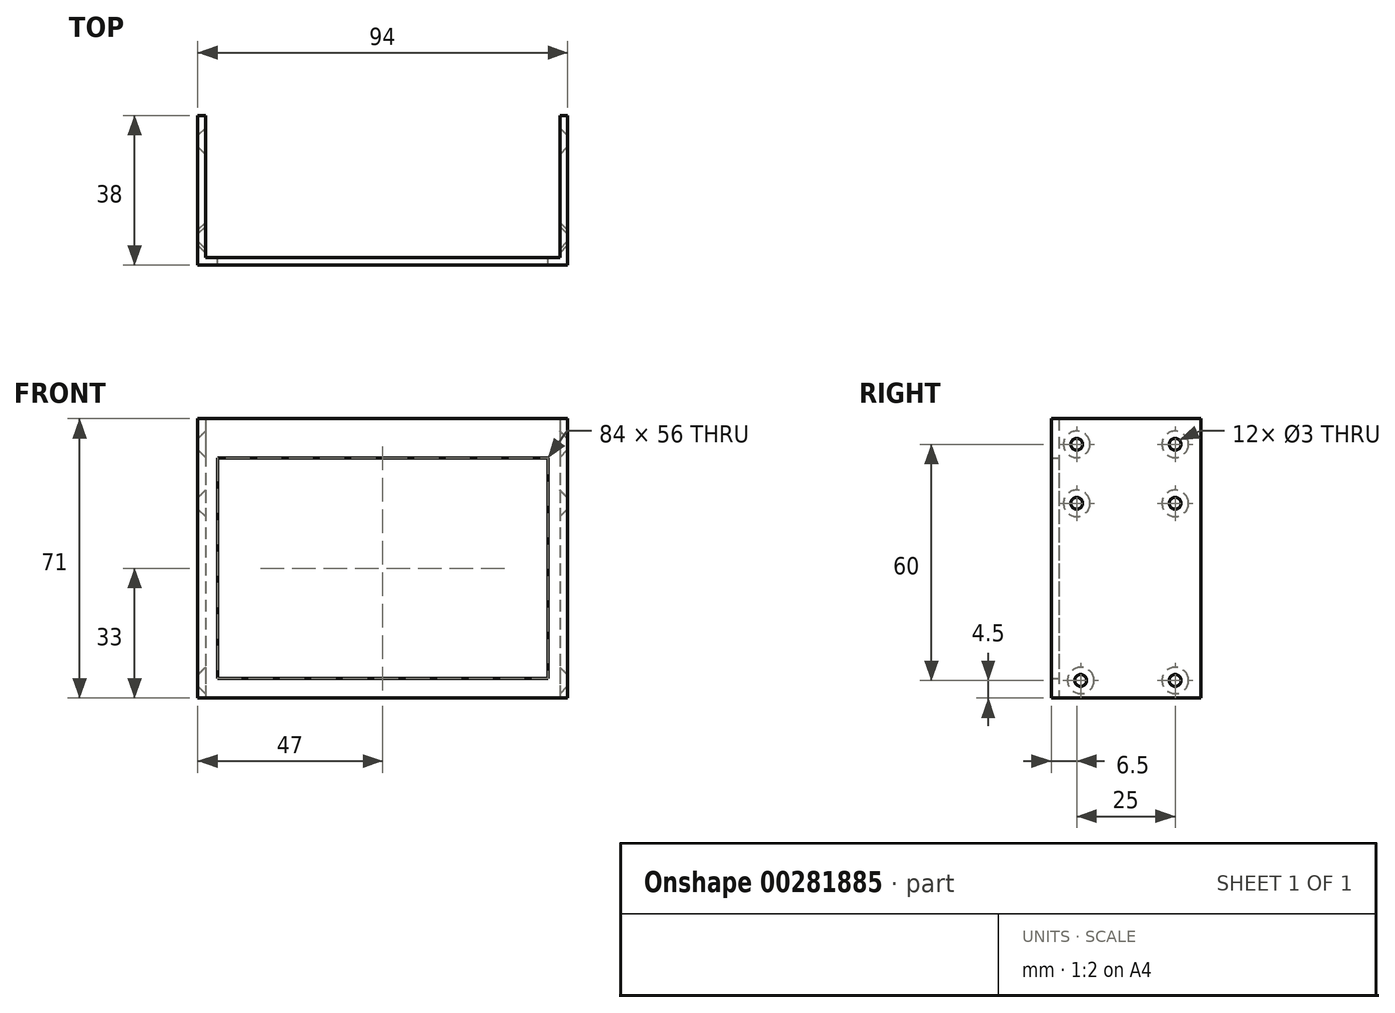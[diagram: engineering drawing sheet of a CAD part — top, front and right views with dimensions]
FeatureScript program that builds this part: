
annotation { "Feature Type Name" : "Feature", "Feature Type Description" : "" }
export const myFeature = defineFeature(function(context is Context, id is Id, definition is map)
    precondition{}
    {
        {
            var Q0;
            Q0=qCreatedBy(makeId("Front.planeOp"),FACE);
            var sketch = newSketch(context, id + "F0", { "sketchPlane" : qUnion([Q0])});
            skLineSegment(sketch, "E0.bottom", {"start": v(47, 35.5) * mm, "end": v(-47, 35.5) * mm});
            skLineSegment(sketch, "E0.top", {"start": v(47, -35.5) * mm, "end": v(-47, -35.5) * mm});
            skLineSegment(sketch, "E0.left", {"start": v(47, 35.5) * mm, "end": v(47, -35.5) * mm});
            skLineSegment(sketch, "E0.right", {"start": v(-47, 35.5) * mm, "end": v(-47, -35.5) * mm});
            skPoint(sketch, "E0.middle", {"position": v(0, 0) * mm});
            skLineSegment(sketch, "E1.bottom", {"start": v(42, 25.5) * mm, "end": v(-42, 25.5) * mm});
            skLineSegment(sketch, "E1.top", {"start": v(42, -30.5) * mm, "end": v(-42, -30.5) * mm});
            skLineSegment(sketch, "E1.left", {"start": v(42, 25.5) * mm, "end": v(42, -30.5) * mm});
            skLineSegment(sketch, "E1.right", {"start": v(-42, 25.5) * mm, "end": v(-42, -30.5) * mm});
            skPoint(sketch, "E1.middle", {"position": v(0, -2.5) * mm});
            skSolve(sketch);
        }
        {
            var Q0;
            Q0=qSketchRegion(id+"F0",true);
            extrude(context, id + "F1", {"entities" : qUnion([Q0]), "depth" : 2 * mm, "symmetric" : true});
        }
        {
            var Q0;
            Q0=makeQuery(id+"F1.opExtrude","CAP_FACE",FACE,{"disambiguationData":[OSD([sQuery(id+"F0.wireOp",EDGE,"E0.bottom"),sQuery(id+"F0.wireOp",EDGE,"E0.top"),sQuery(id+"F0.wireOp",EDGE,"E0.left"),sQuery(id+"F0.wireOp",EDGE,"E0.right"),sQuery(id+"F0.wireOp",EDGE,"SgeA5SFv-ycm6-KkIP-0Kqd-vPRJc91bn5sW.bottom"),sQuery(id+"F0.wireOp",EDGE,"SgeA5SFv-ycm6-KkIP-0Kqd-vPRJc91bn5sW.top"),sQuery(id+"F0.wireOp",EDGE,"SgeA5SFv-ycm6-KkIP-0Kqd-vPRJc91bn5sW.left"),sQuery(id+"F0.wireOp",EDGE,"SgeA5SFv-ycm6-KkIP-0Kqd-vPRJc91bn5sW.right")])],"isStart":true});
            var sketch = newSketch(context, id + "F2", { "sketchPlane" : qUnion([Q0])});
            skLineSegment(sketch, "E2.bottom", {"start": v(-47, 35.5) * mm, "end": v(-45, 35.5) * mm});
            skLineSegment(sketch, "E2.top", {"start": v(-47, -35.5) * mm, "end": v(-45, -35.5) * mm});
            skLineSegment(sketch, "E2.left", {"start": v(-47, 35.5) * mm, "end": v(-47, -35.5) * mm});
            skLineSegment(sketch, "E2.right", {"start": v(-45, 35.5) * mm, "end": v(-45, -35.5) * mm});
            skLineSegment(sketch, "E3.bottom", {"start": v(47, 35.5) * mm, "end": v(45, 35.5) * mm});
            skLineSegment(sketch, "E3.top", {"start": v(47, -35.5) * mm, "end": v(45, -35.5) * mm});
            skLineSegment(sketch, "E3.left", {"start": v(47, 35.5) * mm, "end": v(47, -35.5) * mm});
            skLineSegment(sketch, "E3.right", {"start": v(45, 35.5) * mm, "end": v(45, -35.5) * mm});
            skSolve(sketch);
        }
        {
            var Q0;
            Q0=qSketchRegion(id+"F2",true);
            extrude(context, id + "F3", {"entities" : qUnion([Q0]), "operationType" : NewBodyOperationType.ADD, "depth" : 36 * mm});
        }
        {
            var Q0;
            Q0=makeQuery(id+"F3.boolean.opBoolean","MERGE",FACE,{"derivedFrom":[makeQuery(id+"F1.opExtrude","SWEPT_FACE",FACE,{"disambiguationData":[OSD([sQuery(id+"F0.wireOp",EDGE,"E0.right")])]}),makeQuery(id+"F3.opExtrude","SWEPT_FACE",FACE,{"disambiguationData":[OSD([sQuery(id+"F2.wireOp",EDGE,"E3.left")])]})]});
            var sketch = newSketch(context, id + "F4", { "sketchPlane" : qUnion([Q0])});
            skCircle(sketch, "E4", {"center": v(-30.5, -31) * mm, "radius": 1.5 * mm});
            skCircle(sketch, "E5", {"center": v(-6.5, -31) * mm, "radius": 1.5 * mm});
            skCircle(sketch, "E6", {"center": v(-30.5, 29) * mm, "radius": 1.5 * mm});
            skCircle(sketch, "E7", {"center": v(-5.5, 29) * mm, "radius": 1.5 * mm});
            skLineSegment(sketch, "E8", {"start": v(-30.5, 29) * mm, "end": v(-30.5, -31) * mm, "construction": true});
            skCircle(sketch, "E9", {"center": v(-30.5, 14) * mm, "radius": 1.5 * mm});
            skCircle(sketch, "E10", {"center": v(-5.5, 14) * mm, "radius": 1.5 * mm});
            skSolve(sketch);
        }
        {
            var Q0;
            Q0=qSketchRegion(id+"F4",true);
            extrude(context, id + "F5", {"entities" : qUnion([Q0]), "operationType" : NewBodyOperationType.REMOVE, "oppositeDirection" : true, "depth" : 100 * mm});
        }
        {
            var Q0;
            Q0=makeQuery(id+"F5.boolean.opBoolean","INTERSECT",EDGE,{"derivedFrom":[makeQuery(id+"F3.opExtrude","SWEPT_FACE",FACE,{"disambiguationData":[OSD([sQuery(id+"F2.wireOp",EDGE,"E3.right")])]}),makeQuery(id+"F5.opExtrude","SWEPT_FACE",FACE,{"disambiguationData":[OSD([sQuery(id+"F4.wireOp",EDGE,"E6")])]})]});
            var Q1;
            Q1=makeQuery(id+"F5.boolean.opBoolean","INTERSECT",EDGE,{"derivedFrom":[makeQuery(id+"F3.opExtrude","SWEPT_FACE",FACE,{"disambiguationData":[OSD([sQuery(id+"F2.wireOp",EDGE,"E3.right")])]}),makeQuery(id+"F5.opExtrude","SWEPT_FACE",FACE,{"disambiguationData":[OSD([sQuery(id+"F4.wireOp",EDGE,"E9")])]})]});
            var Q2;
            Q2=makeQuery(id+"F5.boolean.opBoolean","INTERSECT",EDGE,{"derivedFrom":[makeQuery(id+"F3.opExtrude","SWEPT_FACE",FACE,{"disambiguationData":[OSD([sQuery(id+"F2.wireOp",EDGE,"E3.right")])]}),makeQuery(id+"F5.opExtrude","SWEPT_FACE",FACE,{"disambiguationData":[OSD([sQuery(id+"F4.wireOp",EDGE,"E7")])]})]});
            var Q3;
            Q3=makeQuery(id+"F5.boolean.opBoolean","INTERSECT",EDGE,{"derivedFrom":[makeQuery(id+"F3.opExtrude","SWEPT_FACE",FACE,{"disambiguationData":[OSD([sQuery(id+"F2.wireOp",EDGE,"E2.right")])]}),makeQuery(id+"F5.opExtrude","SWEPT_FACE",FACE,{"disambiguationData":[OSD([sQuery(id+"F4.wireOp",EDGE,"E7")])]})]});
            var Q4;
            Q4=makeQuery(id+"F5.boolean.opBoolean","INTERSECT",EDGE,{"derivedFrom":[makeQuery(id+"F3.opExtrude","SWEPT_FACE",FACE,{"disambiguationData":[OSD([sQuery(id+"F2.wireOp",EDGE,"E2.right")])]}),makeQuery(id+"F5.opExtrude","SWEPT_FACE",FACE,{"disambiguationData":[OSD([sQuery(id+"F4.wireOp",EDGE,"E10")])]})]});
            var Q5;
            Q5=makeQuery(id+"F5.boolean.opBoolean","INTERSECT",EDGE,{"derivedFrom":[makeQuery(id+"F3.opExtrude","SWEPT_FACE",FACE,{"disambiguationData":[OSD([sQuery(id+"F2.wireOp",EDGE,"E2.right")])]}),makeQuery(id+"F5.opExtrude","SWEPT_FACE",FACE,{"disambiguationData":[OSD([sQuery(id+"F4.wireOp",EDGE,"E6")])]})]});
            var Q6;
            Q6=makeQuery(id+"F5.boolean.opBoolean","INTERSECT",EDGE,{"derivedFrom":[makeQuery(id+"F3.opExtrude","SWEPT_FACE",FACE,{"disambiguationData":[OSD([sQuery(id+"F2.wireOp",EDGE,"E2.right")])]}),makeQuery(id+"F5.opExtrude","SWEPT_FACE",FACE,{"disambiguationData":[OSD([sQuery(id+"F4.wireOp",EDGE,"E9")])]})]});
            var Q7;
            Q7=makeQuery(id+"F5.boolean.opBoolean","INTERSECT",EDGE,{"derivedFrom":[makeQuery(id+"F3.opExtrude","SWEPT_FACE",FACE,{"disambiguationData":[OSD([sQuery(id+"F2.wireOp",EDGE,"E3.right")])]}),makeQuery(id+"F5.opExtrude","SWEPT_FACE",FACE,{"disambiguationData":[OSD([sQuery(id+"F4.wireOp",EDGE,"E10")])]})]});
            var Q8;
            Q8=makeQuery(id+"F5.boolean.opBoolean","INTERSECT",EDGE,{"derivedFrom":[makeQuery(id+"F3.opExtrude","SWEPT_FACE",FACE,{"disambiguationData":[OSD([sQuery(id+"F2.wireOp",EDGE,"E2.right")])]}),makeQuery(id+"F5.opExtrude","SWEPT_FACE",FACE,{"disambiguationData":[OSD([sQuery(id+"F4.wireOp",EDGE,"E5")])]})]});
            var Q9;
            Q9=makeQuery(id+"F5.boolean.opBoolean","INTERSECT",EDGE,{"derivedFrom":[makeQuery(id+"F3.opExtrude","SWEPT_FACE",FACE,{"disambiguationData":[OSD([sQuery(id+"F2.wireOp",EDGE,"E2.right")])]}),makeQuery(id+"F5.opExtrude","SWEPT_FACE",FACE,{"disambiguationData":[OSD([sQuery(id+"F4.wireOp",EDGE,"E4")])]})]});
            var Q10;
            Q10=makeQuery(id+"F5.boolean.opBoolean","INTERSECT",EDGE,{"derivedFrom":[makeQuery(id+"F3.opExtrude","SWEPT_FACE",FACE,{"disambiguationData":[OSD([sQuery(id+"F2.wireOp",EDGE,"E3.right")])]}),makeQuery(id+"F5.opExtrude","SWEPT_FACE",FACE,{"disambiguationData":[OSD([sQuery(id+"F4.wireOp",EDGE,"E5")])]})]});
            var Q11;
            Q11=makeQuery(id+"F5.boolean.opBoolean","INTERSECT",EDGE,{"derivedFrom":[makeQuery(id+"F3.opExtrude","SWEPT_FACE",FACE,{"disambiguationData":[OSD([sQuery(id+"F2.wireOp",EDGE,"E3.right")])]}),makeQuery(id+"F5.opExtrude","SWEPT_FACE",FACE,{"disambiguationData":[OSD([sQuery(id+"F4.wireOp",EDGE,"E4")])]})]});
            chamfer(context, id + "F6", {"entities" : qUnion([Q0, Q1, Q2, Q3, Q4, Q5, Q6, Q7, Q8, Q9, Q10, Q11]), "width" : 1.87 * mm, "tangentPropagation" : true});
        }
    });
